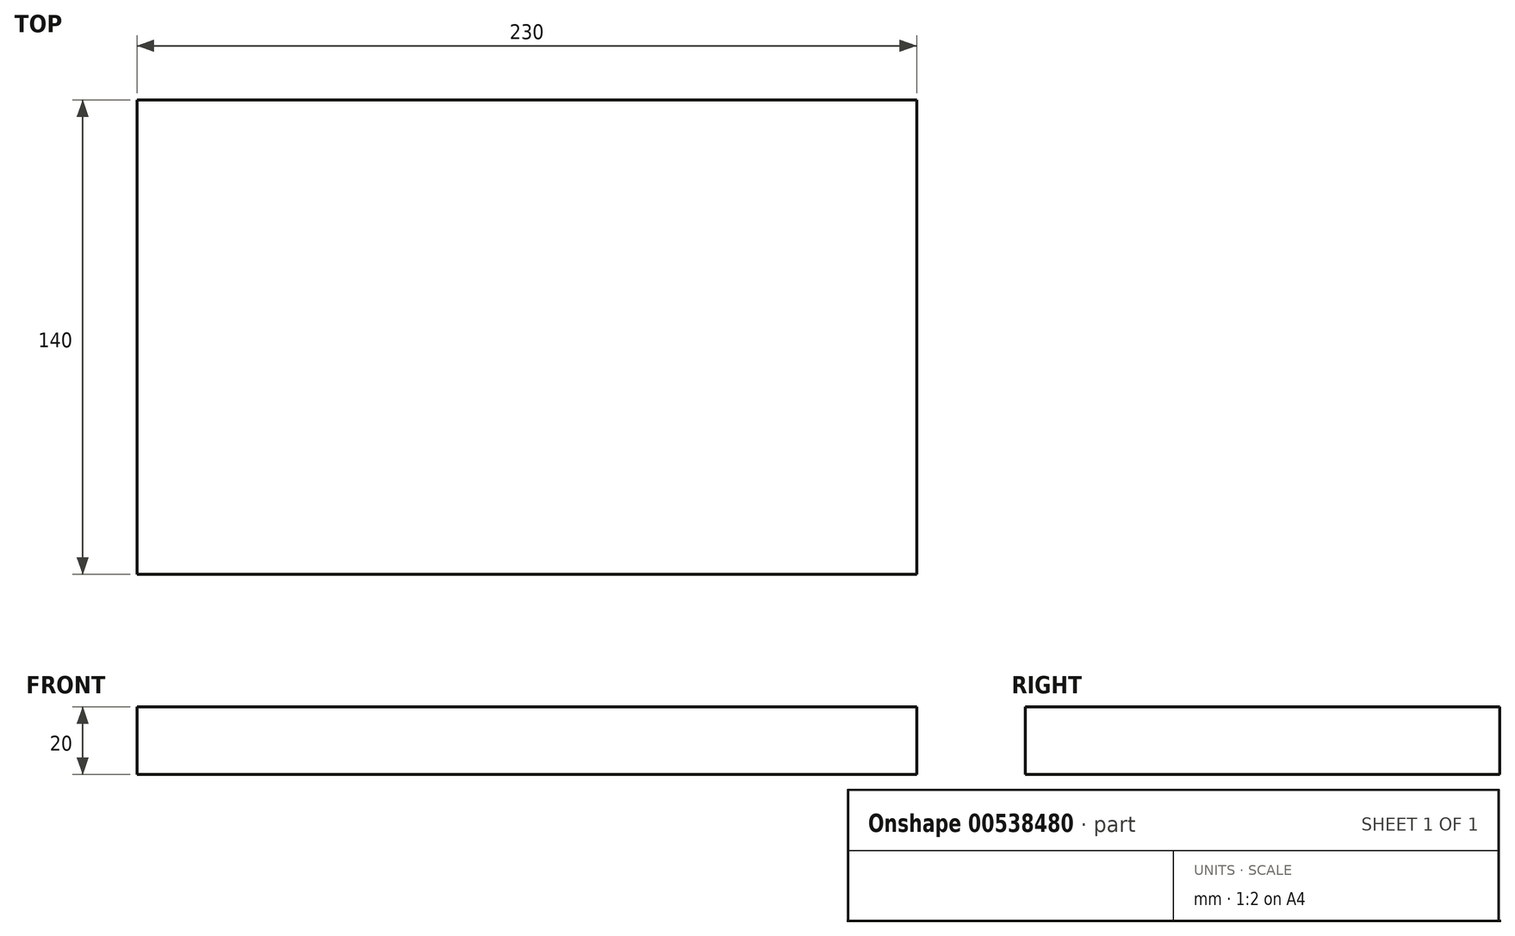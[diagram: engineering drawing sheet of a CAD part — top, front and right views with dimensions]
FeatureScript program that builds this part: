
annotation { "Feature Type Name" : "Feature", "Feature Type Description" : "" }
export const myFeature = defineFeature(function(context is Context, id is Id, definition is map)
    precondition{}
    {
        {
            var Q0;
            Q0=qCreatedBy(makeId("Top.planeOp"),FACE);
            var sketch = newSketch(context, id + "F0", { "sketchPlane" : qUnion([Q0])});
            skLineSegment(sketch, "E0.bottom", {"start": v(-115, 70) * mm, "end": v(115, 70) * mm});
            skLineSegment(sketch, "E0.top", {"start": v(-115, -70) * mm, "end": v(115, -70) * mm});
            skLineSegment(sketch, "E0.left", {"start": v(-115, 70) * mm, "end": v(-115, -70) * mm});
            skLineSegment(sketch, "E0.right", {"start": v(115, 70) * mm, "end": v(115, -70) * mm});
            skPoint(sketch, "E0.middle", {"position": v(0, 0) * mm});
            skSolve(sketch);
        }
        {
            var Q0;
            Q0=makeQuery(id+"F0.imprint","IMPRINT",FACE,{"disambiguationData":[TD([[makeQuery(id+"F0.imprint","IMPRINT",EDGE,{"derivedFrom":sQuery(id+"F0.wireOp",EDGE,"E0.bottom")}),-1.0]])]});
            extrude(context, id + "F1", {"entities" : qUnion([Q0]), "depth" : 20 * mm, "offsetDistance" : 25 * mm});
        }
    });
